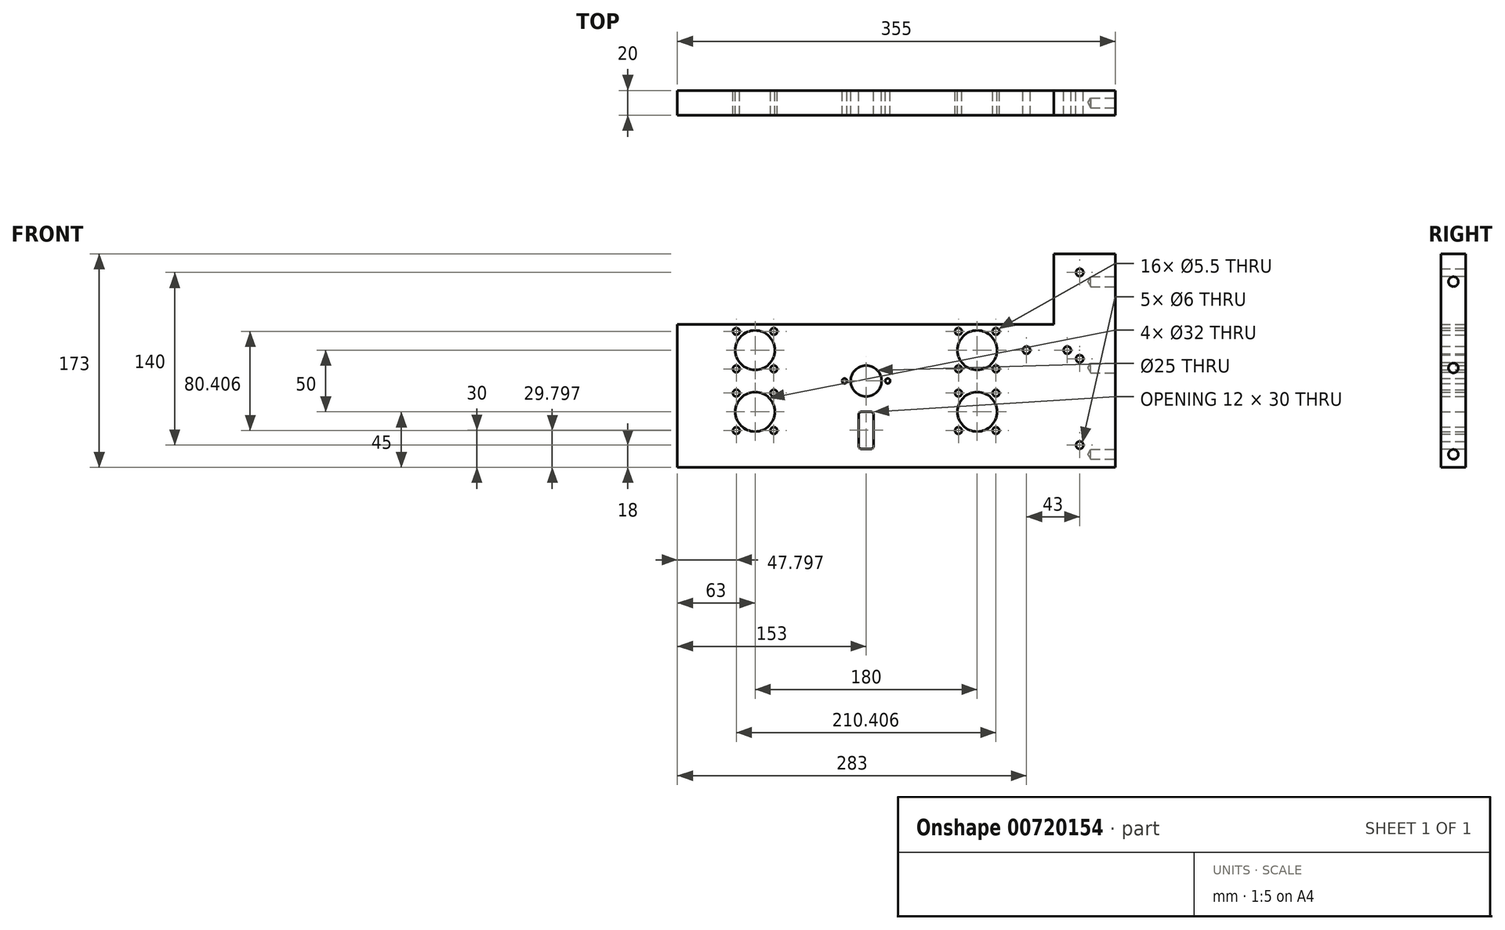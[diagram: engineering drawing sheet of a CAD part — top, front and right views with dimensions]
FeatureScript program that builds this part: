
annotation { "Feature Type Name" : "Feature", "Feature Type Description" : "" }
export const myFeature = defineFeature(function(context is Context, id is Id, definition is map)
    precondition{}
    {
        {
            var Q0;
            Q0=qCreatedBy(makeId("Front.planeOp"),FACE);
            var sketch = newSketch(context, id + "F0", { "sketchPlane" : qUnion([Q0])});
            skLineSegment(sketch, "E0", {"start": v(0, 0) * mm, "end": v(0, 115) * mm});
            skLineSegment(sketch, "E1", {"start": v(0, 115) * mm, "end": v(305, 115) * mm, "construction": true});
            skLineSegment(sketch, "E2", {"start": v(305, 115) * mm, "end": v(305, 173) * mm});
            skLineSegment(sketch, "E3", {"start": v(305, 173) * mm, "end": v(355, 173) * mm});
            skLineSegment(sketch, "E4", {"start": v(355, 173) * mm, "end": v(355, 0) * mm});
            skLineSegment(sketch, "E5", {"start": v(355, 0) * mm, "end": v(0, 0) * mm});
            skCircle(sketch, "E6", {"center": v(153, 70) * mm, "radius": 12.5 * mm});
            skCircle(sketch, "E7", {"center": v(63, 95) * mm, "radius": 16 * mm});
            skArc(sketch, "E8", {"start": v(47.8, 110.2) * mm, "mid": v(63, 73.5) * mm, "end": v(78.2, 110.2) * mm, "construction": true});
            skCircle(sketch, "E9", {"center": v(47.8, 110.2) * mm, "radius": 2.75 * mm});
            skCircle(sketch, "E10", {"center": v(78.2, 110.2) * mm, "radius": 2.75 * mm});
            skCircle(sketch, "E11", {"center": v(78.2, 79.8) * mm, "radius": 2.75 * mm});
            skCircle(sketch, "E12", {"center": v(47.8, 79.8) * mm, "radius": 2.75 * mm});
            skArc(sketch, "E13.trimOffspring", {"start": v(76.14, 112.02) * mm, "mid": v(63, 116.5) * mm, "end": v(49.86, 112.02) * mm, "construction": true});
            skLineSegment(sketch, "E14", {"start": v(153, 70) * mm, "end": v(153, 34.16) * mm, "construction": true});
            skLineSegment(sketch, "E15", {"start": v(128.05, 70) * mm, "end": v(153, 70) * mm, "construction": true});
            skCircle(sketch, "E16.MirrorC", {"center": v(78.2, 60.2) * mm, "radius": 2.75 * mm});
            skCircle(sketch, "E17.MirrorC", {"center": v(63, 45) * mm, "radius": 16 * mm});
            skCircle(sketch, "E18.MirrorC", {"center": v(47.8, 60.2) * mm, "radius": 2.75 * mm});
            skCircle(sketch, "E19.MirrorC", {"center": v(47.8, 29.8) * mm, "radius": 2.75 * mm});
            skCircle(sketch, "E20.MirrorC", {"center": v(78.2, 29.8) * mm, "radius": 2.75 * mm});
            skCircle(sketch, "E21.MirrorC", {"center": v(227.8, 29.8) * mm, "radius": 2.75 * mm});
            skCircle(sketch, "E22.MirrorC", {"center": v(243, 45) * mm, "radius": 16 * mm});
            skCircle(sketch, "E23.MirrorC", {"center": v(227.8, 60.2) * mm, "radius": 2.75 * mm});
            skCircle(sketch, "E24.MirrorC", {"center": v(258.2, 60.2) * mm, "radius": 2.75 * mm});
            skCircle(sketch, "E25.MirrorC", {"center": v(258.2, 29.8) * mm, "radius": 2.75 * mm});
            skCircle(sketch, "E26.MirrorC", {"center": v(258.2, 79.8) * mm, "radius": 2.75 * mm});
            skCircle(sketch, "E27.MirrorC", {"center": v(227.8, 79.8) * mm, "radius": 2.75 * mm});
            skCircle(sketch, "E28.MirrorC", {"center": v(243, 95) * mm, "radius": 16 * mm});
            skCircle(sketch, "E29.MirrorC", {"center": v(227.8, 110.2) * mm, "radius": 2.75 * mm});
            skCircle(sketch, "E30.MirrorC", {"center": v(258.2, 110.2) * mm, "radius": 2.75 * mm});
            skLineSegment(sketch, "E31.bottom", {"start": v(149, 45) * mm, "end": v(157, 45) * mm});
            skLineSegment(sketch, "E31.top", {"start": v(149, 15) * mm, "end": v(157, 15) * mm});
            skLineSegment(sketch, "E31.left", {"start": v(147, 43) * mm, "end": v(147, 17) * mm});
            skLineSegment(sketch, "E31.right", {"start": v(159, 43) * mm, "end": v(159, 17) * mm});
            skPoint(sketch, "E32.visualSharp", {"position": v(147, 15) * mm});
            skArc(sketch, "E32.filletArc", {"start": v(147, 17) * mm, "mid": v(147.59, 15.59) * mm, "end": v(149, 15) * mm});
            skPoint(sketch, "E33.visualSharp", {"position": v(159, 15) * mm});
            skArc(sketch, "E33.filletArc", {"start": v(157, 15) * mm, "mid": v(158.41, 15.59) * mm, "end": v(159, 17) * mm});
            skPoint(sketch, "E34.visualSharp", {"position": v(147, 45) * mm});
            skArc(sketch, "E34.filletArc", {"start": v(149, 45) * mm, "mid": v(147.59, 44.41) * mm, "end": v(147, 43) * mm});
            skPoint(sketch, "E35.visualSharp", {"position": v(159, 45) * mm});
            skArc(sketch, "E35.filletArc", {"start": v(159, 43) * mm, "mid": v(158.41, 44.41) * mm, "end": v(157, 45) * mm});
            skCircle(sketch, "E36", {"center": v(170.5, 70) * mm, "radius": 2 * mm});
            skCircle(sketch, "E37.MirrorC", {"center": v(135.5, 70) * mm, "radius": 2 * mm});
            skCircle(sketch, "E38", {"center": v(326, 158) * mm, "radius": 3 * mm});
            skCircle(sketch, "E39.0.1.0", {"center": v(326, 88) * mm, "radius": 3 * mm});
            skCircle(sketch, "E39.0.2.0", {"center": v(326, 18) * mm, "radius": 3 * mm});
            skLineSegment(sketch, "E39.direction1", {"start": v(326, 158) * mm, "end": v(351, 158) * mm, "construction": true});
            skLineSegment(sketch, "E39.direction2", {"start": v(326, 158) * mm, "end": v(326, 88) * mm, "construction": true});
            skCircle(sketch, "E40", {"center": v(316, 95) * mm, "radius": 3 * mm});
            skCircle(sketch, "E41", {"center": v(283, 95) * mm, "radius": 3 * mm});
            skLineSegment(sketch, "E42", {"start": v(0, 115) * mm, "end": v(0, 116) * mm});
            skLineSegment(sketch, "E43", {"start": v(0, 116) * mm, "end": v(305, 116) * mm});
            skSolve(sketch);
        }
        {
            var Q0;
            Q0 = qSketchRegion(id + "F0", true);
            extrude(context, id + "F1", {"entities" : qUnion([Q0]), "depth" : 20 * mm, "offsetDistance" : 25 * mm});
        }
        {
            var Q0;
            Q0=makeQuery(id+"F1.opExtrude","SWEPT_FACE",FACE,{"disambiguationData":[OSD([sQuery(id+"F0.wireOp",EDGE,"E4")])]});
            var sketch = newSketch(context, id + "F2", { "sketchPlane" : qUnion([Q0])});
            skCircle(sketch, "E44", {"center": v(-10, 150.5) * mm, "radius": 4 * mm});
            skPoint(sketch, "E44.centerSnap0", {"position": v(-10, 173) * mm});
            skCircle(sketch, "E45", {"center": v(-10, 80.5) * mm, "radius": 4 * mm});
            skCircle(sketch, "E46", {"center": v(-10, 10.5) * mm, "radius": 4 * mm});
            skSolve(sketch);
        }
        {
            var Q0;
            Q0=sQuery(id+"F2.wireOp",VERTEX,"E44.center");
            var Q1;
            Q1=sQuery(id+"F2.wireOp",VERTEX,"E45.center");
            var Q2;
            Q2=sQuery(id+"F2.wireOp",VERTEX,"E46.center");
            var Q3;
            Q3=makeQuery(id+"F1.opExtrude","SWEPT_BODY",BODY,{"disambiguationData":[OSD([sQuery(id+"F0.wireOp",EDGE,"E0"),sQuery(id+"F0.wireOp",EDGE,"E1"),sQuery(id+"F0.wireOp",EDGE,"E2"),sQuery(id+"F0.wireOp",EDGE,"E3"),sQuery(id+"F0.wireOp",EDGE,"E4"),sQuery(id+"F0.wireOp",EDGE,"E5"),sQuery(id+"F0.wireOp",EDGE,"E6"),sQuery(id+"F0.wireOp",EDGE,"E7"),sQuery(id+"F0.wireOp",EDGE,"E9"),sQuery(id+"F0.wireOp",EDGE,"E10"),sQuery(id+"F0.wireOp",EDGE,"E11"),sQuery(id+"F0.wireOp",EDGE,"E12"),sQuery(id+"F0.wireOp",EDGE,"E16.MirrorC"),sQuery(id+"F0.wireOp",EDGE,"E17.MirrorC"),sQuery(id+"F0.wireOp",EDGE,"E18.MirrorC"),sQuery(id+"F0.wireOp",EDGE,"E19.MirrorC"),sQuery(id+"F0.wireOp",EDGE,"E20.MirrorC"),sQuery(id+"F0.wireOp",EDGE,"E21.MirrorC"),sQuery(id+"F0.wireOp",EDGE,"E22.MirrorC"),sQuery(id+"F0.wireOp",EDGE,"E23.MirrorC"),sQuery(id+"F0.wireOp",EDGE,"E24.MirrorC"),sQuery(id+"F0.wireOp",EDGE,"E25.MirrorC"),sQuery(id+"F0.wireOp",EDGE,"E26.MirrorC"),sQuery(id+"F0.wireOp",EDGE,"E27.MirrorC"),sQuery(id+"F0.wireOp",EDGE,"E28.MirrorC"),sQuery(id+"F0.wireOp",EDGE,"E29.MirrorC"),sQuery(id+"F0.wireOp",EDGE,"E30.MirrorC"),sQuery(id+"F0.wireOp",EDGE,"E31.bottom"),sQuery(id+"F0.wireOp",EDGE,"E31.top"),sQuery(id+"F0.wireOp",EDGE,"E31.left"),sQuery(id+"F0.wireOp",EDGE,"E31.right"),sQuery(id+"F0.wireOp",EDGE,"E32.filletArc"),sQuery(id+"F0.wireOp",EDGE,"E33.filletArc"),sQuery(id+"F0.wireOp",EDGE,"E34.filletArc"),sQuery(id+"F0.wireOp",EDGE,"E35.filletArc"),sQuery(id+"F0.wireOp",EDGE,"E36"),sQuery(id+"F0.wireOp",EDGE,"E37.MirrorC"),sQuery(id+"F0.wireOp",EDGE,"E38"),sQuery(id+"F0.wireOp",EDGE,"E39.0.1.0"),sQuery(id+"F0.wireOp",EDGE,"E39.0.2.0"),sQuery(id+"F0.wireOp",EDGE,"E40"),sQuery(id+"F0.wireOp",EDGE,"E41")])]});
            hole(context, id + "F3", {"style" : HoleStyle.SIMPLE, "endStyle" : HoleEndStyle.BLIND, "holeDiameter" : 8 * mm, "majorDiameter" : 5 * mm, "holeDepth" : 20 * mm, "isTappedThrough" : true, "tappedDepth" : 12 * mm, "tapClearance" : 3, "startFromSketch" : true, "locations" : qUnion([Q0, Q1, Q2]), "scope" : qUnion([Q3])});
        }
    });
